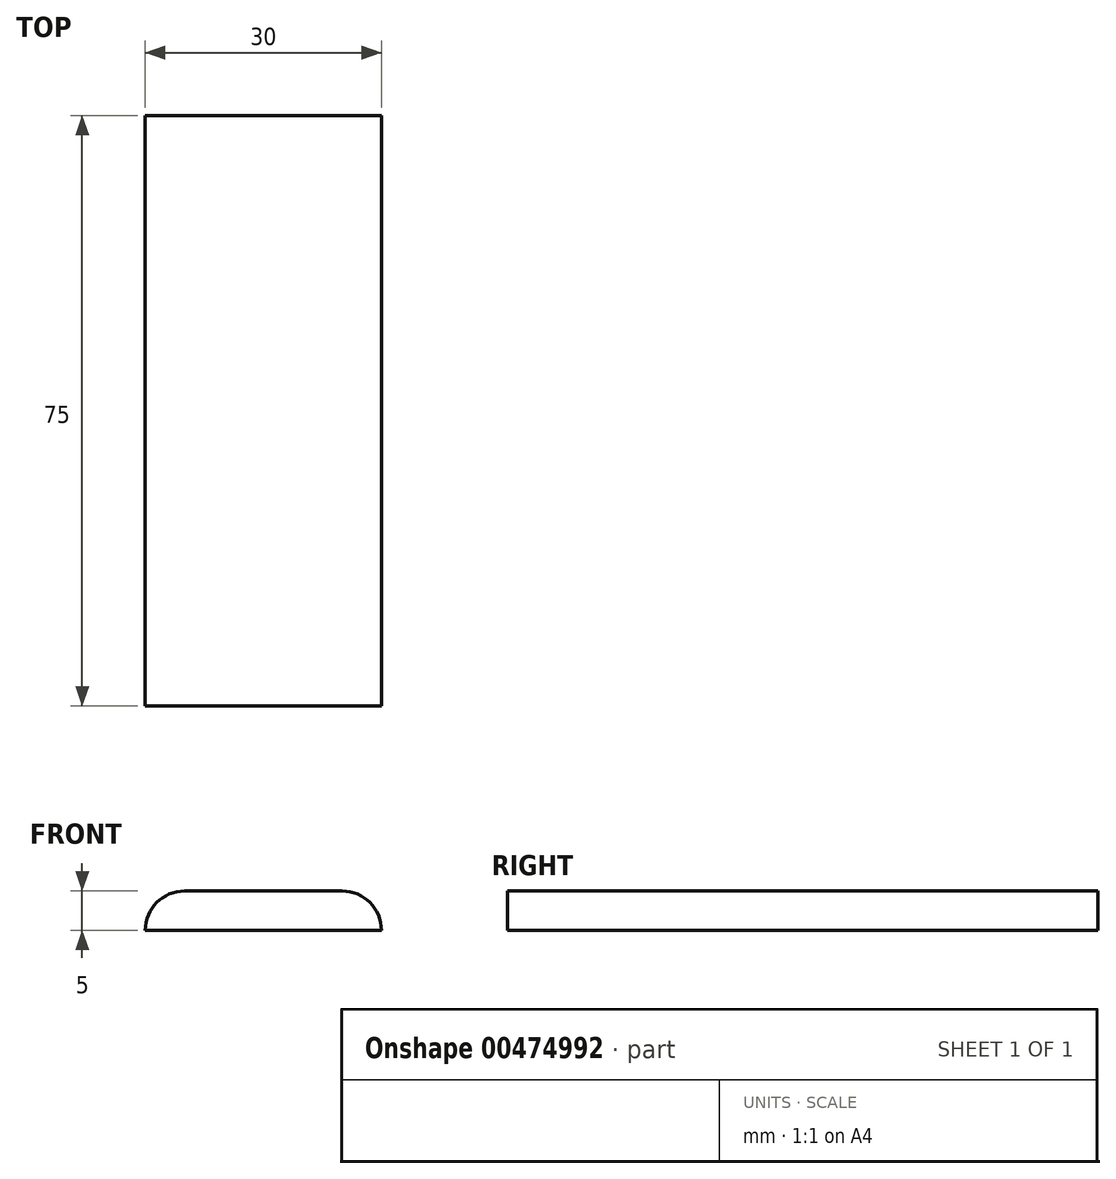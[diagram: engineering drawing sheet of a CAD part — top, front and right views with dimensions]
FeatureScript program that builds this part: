
annotation { "Feature Type Name" : "Feature", "Feature Type Description" : "" }
export const myFeature = defineFeature(function(context is Context, id is Id, definition is map)
    precondition{}
    {
        {
            var Q0;
            Q0=qCreatedBy(makeId("Top.planeOp"),FACE);
            var sketch = newSketch(context, id + "F0", { "sketchPlane" : qUnion([Q0])});
            skLineSegment(sketch, "E0.bottom", {"start": v(-15, 37.5) * mm, "end": v(15, 37.5) * mm});
            skLineSegment(sketch, "E0.top", {"start": v(-15, -37.5) * mm, "end": v(15, -37.5) * mm});
            skLineSegment(sketch, "E0.left", {"start": v(-15, 37.5) * mm, "end": v(-15, -37.5) * mm});
            skLineSegment(sketch, "E0.right", {"start": v(15, 37.5) * mm, "end": v(15, -37.5) * mm});
            skPoint(sketch, "E0.middle", {"position": v(0, 0) * mm});
            skSolve(sketch);
        }
        {
            var Q0;
            Q0=makeQuery(id+"F0.imprint","IMPRINT",FACE,{"disambiguationData":[TD([[makeQuery(id+"F0.imprint","IMPRINT",EDGE,{"derivedFrom":sQuery(id+"F0.wireOp",EDGE,"E0.bottom")}),-1.0]])]});
            extrude(context, id + "F1", {"entities" : qUnion([Q0]), "endBound" : BoundingType.SYMMETRIC, "depth" : 5 * mm});
        }
        {
            var Q0;
            Q0=makeQuery(id+"F1.opExtrude","CAP_EDGE",EDGE,{"disambiguationData":[OSD([sQuery(id+"F0.wireOp",EDGE,"E0.right")])],"isStart":false});
            var Q1;
            Q1=makeQuery(id+"F1.opExtrude","CAP_EDGE",EDGE,{"disambiguationData":[OSD([sQuery(id+"F0.wireOp",EDGE,"E0.left")])],"isStart":false});
            fillet(context, id + "F2", {"entities" : qUnion([Q0, Q1]), "radius" : 5 * mm, "tangentPropagation" : true, "allowEdgeOverflow" : false});
        }
    });
